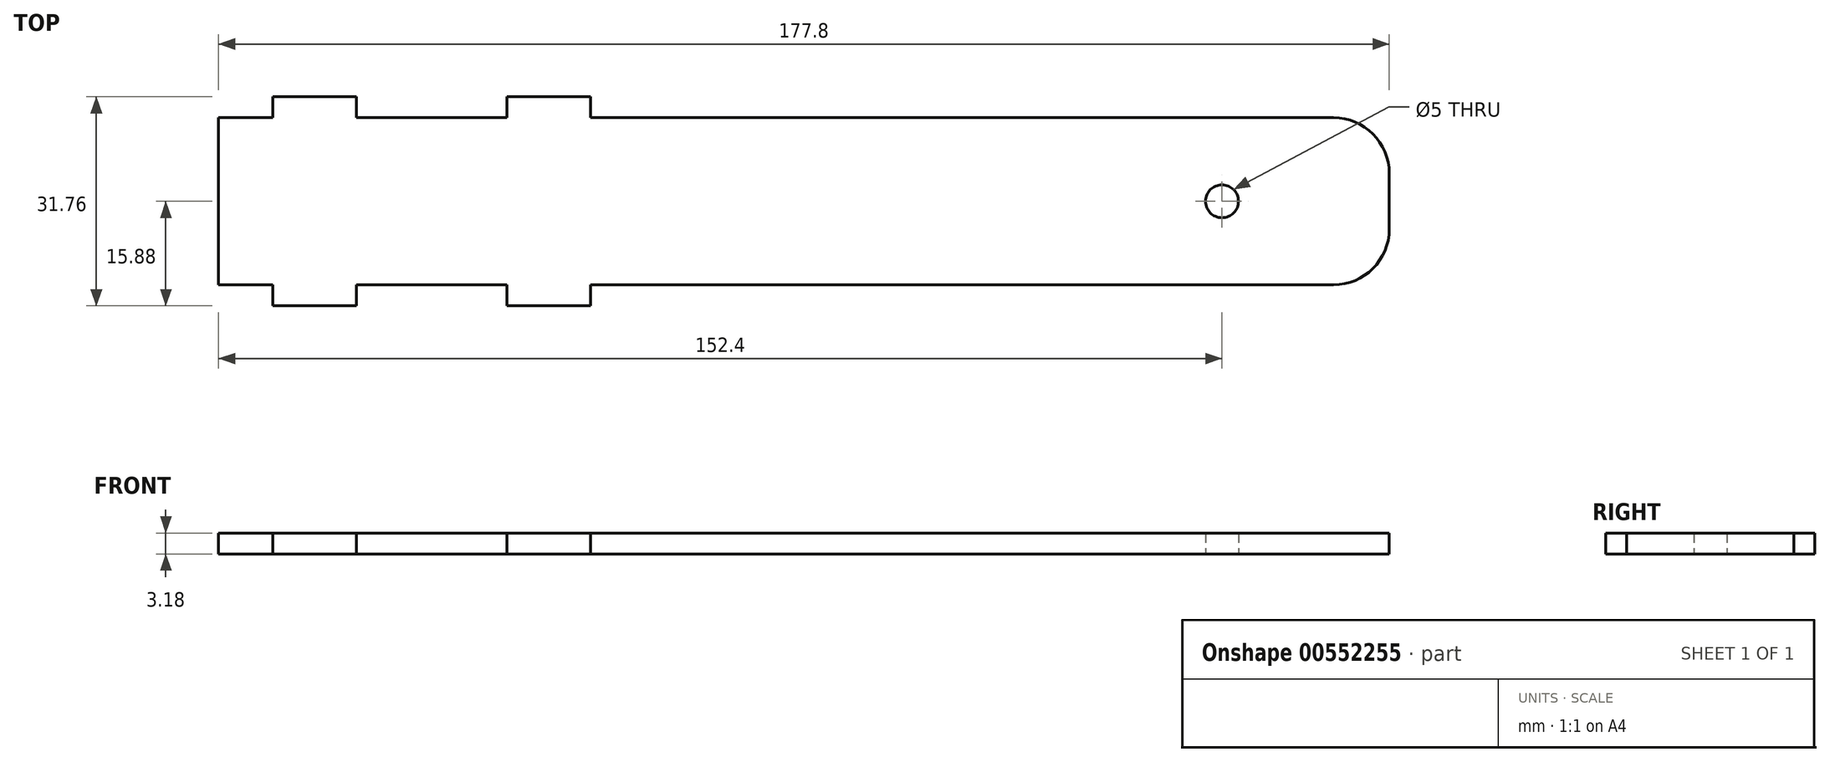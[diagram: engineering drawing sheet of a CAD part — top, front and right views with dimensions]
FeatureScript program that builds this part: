
annotation { "Feature Type Name" : "Feature", "Feature Type Description" : "" }
export const myFeature = defineFeature(function(context is Context, id is Id, definition is map)
    precondition{}
    {
        {
            var Q0;
            Q0=qCreatedBy(makeId("Top.planeOp"),FACE);
            var sketch = newSketch(context, id + "F0", { "sketchPlane" : qUnion([Q0])});
            skLineSegment(sketch, "E0.left", {"start": v(-76.2, 12.7) * mm, "end": v(-76.2, -12.7) * mm});
            skPoint(sketch, "E0.middle", {"position": v(0, 0) * mm});
            skLineSegment(sketch, "E1", {"start": v(-76.2, -12.7) * mm, "end": v(-69.85, -12.7) * mm});
            skLineSegment(sketch, "E2.bottom", {"start": v(-76.2, 12.7) * mm, "end": v(-69.85, 12.7) * mm});
            skLineSegment(sketch, "E3", {"start": v(-55.25, -12.7) * mm, "end": v(-55.25, -15.87) * mm});
            skLineSegment(sketch, "E4.bottom", {"start": v(-55.25, -15.87) * mm, "end": v(-67.95, -15.87) * mm});
            skLineSegment(sketch, "E4.left", {"start": v(-55.25, -15.87) * mm, "end": v(-55.25, -12.7) * mm});
            skLineSegment(sketch, "E4.right", {"start": v(-67.95, -15.87) * mm, "end": v(-67.95, -12.7) * mm});
            skLineSegment(sketch, "E5", {"start": v(-67.95, 12.7) * mm, "end": v(-67.95, 15.88) * mm});
            skLineSegment(sketch, "E6.bottom", {"start": v(-67.95, 15.88) * mm, "end": v(-55.25, 15.88) * mm});
            skLineSegment(sketch, "E6.left", {"start": v(-67.95, 15.88) * mm, "end": v(-67.95, 12.7) * mm});
            skLineSegment(sketch, "E6.right", {"start": v(-55.25, 15.88) * mm, "end": v(-55.25, 12.7) * mm});
            skLineSegment(sketch, "E7", {"start": v(-53.34, 12.7) * mm, "end": v(-34.3, 12.7) * mm});
            skLineSegment(sketch, "E8.bottom", {"start": v(-53.34, -12.7) * mm, "end": v(-34.3, -12.7) * mm});
            skLineSegment(sketch, "E9", {"start": v(-32.39, 12.7) * mm, "end": v(-32.39, 15.88) * mm});
            skLineSegment(sketch, "E10.bottom", {"start": v(-32.39, 15.88) * mm, "end": v(-19.69, 15.88) * mm});
            skLineSegment(sketch, "E10.left", {"start": v(-32.39, 15.88) * mm, "end": v(-32.39, 12.7) * mm});
            skLineSegment(sketch, "E10.right", {"start": v(-19.69, 15.88) * mm, "end": v(-19.69, 12.7) * mm});
            skLineSegment(sketch, "E11", {"start": v(-19.69, -12.7) * mm, "end": v(-19.69, -15.87) * mm});
            skLineSegment(sketch, "E12.bottom", {"start": v(-19.69, -15.87) * mm, "end": v(-32.39, -15.87) * mm});
            skLineSegment(sketch, "E12.left", {"start": v(-19.69, -15.87) * mm, "end": v(-19.69, -12.7) * mm});
            skLineSegment(sketch, "E12.right", {"start": v(-32.39, -15.87) * mm, "end": v(-32.39, -12.7) * mm});
            skLineSegment(sketch, "E13", {"start": v(-69.85, 12.7) * mm, "end": v(-67.95, 12.7) * mm});
            skLineSegment(sketch, "E14", {"start": v(-55.25, 12.7) * mm, "end": v(-53.34, 12.7) * mm});
            skLineSegment(sketch, "E15", {"start": v(-34.3, 12.7) * mm, "end": v(-32.39, 12.7) * mm});
            skLineSegment(sketch, "E16", {"start": v(-69.85, -12.7) * mm, "end": v(-67.95, -12.7) * mm});
            skLineSegment(sketch, "E17", {"start": v(-55.25, -12.7) * mm, "end": v(-53.34, -12.7) * mm});
            skLineSegment(sketch, "E18", {"start": v(-34.3, -12.7) * mm, "end": v(-32.39, -12.7) * mm});
            skLineSegment(sketch, "E19", {"start": v(-19.69, 12.7) * mm, "end": v(76.2, 12.7) * mm});
            skLineSegment(sketch, "E20", {"start": v(62.48, -12.7) * mm, "end": v(-19.69, -12.7) * mm});
            skLineSegment(sketch, "E21", {"start": v(76.2, 12.7) * mm, "end": v(93.13, 12.7) * mm});
            skLineSegment(sketch, "E22", {"start": v(89.92, -12.7) * mm, "end": v(93.13, -12.7) * mm});
            skLineSegment(sketch, "E23", {"start": v(101.6, 4.23) * mm, "end": v(101.6, -4.23) * mm});
            skCircle(sketch, "E24", {"center": v(76.2, 0) * mm, "radius": 2.5 * mm});
            skPoint(sketch, "E25.visualSharp", {"position": v(101.6, 12.7) * mm});
            skArc(sketch, "E25.filletArc", {"start": v(101.6, 4.23) * mm, "mid": v(99.12, 10.22) * mm, "end": v(93.13, 12.7) * mm});
            skPoint(sketch, "E26.visualSharp", {"position": v(101.6, -12.7) * mm});
            skArc(sketch, "E26.filletArc", {"start": v(93.13, -12.7) * mm, "mid": v(99.12, -10.22) * mm, "end": v(101.6, -4.23) * mm});
            skLineSegment(sketch, "E27.bottom", {"start": v(88.93, -12.7) * mm, "end": v(63.47, -12.7) * mm});
            skLineSegment(sketch, "E28", {"start": v(89.92, -12.7) * mm, "end": v(88.93, -12.7) * mm});
            skLineSegment(sketch, "E29", {"start": v(63.47, -12.7) * mm, "end": v(62.48, -12.7) * mm});
            skSolve(sketch);
        }
        {
            var Q0;
            Q0 = qSketchRegion(id + "F0", true);
            extrude(context, id + "F1", {"entities" : qUnion([Q0]), "depth" : 3.17 * mm, "offsetDistance" : 25.4 * mm});
        }
    });
